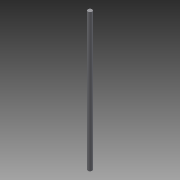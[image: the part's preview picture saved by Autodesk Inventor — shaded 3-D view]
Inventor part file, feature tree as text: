
AUTODESK INVENTOR PART (.ipt)
format: ipt  version: 2013 (Build 170138000, 138)  size: 60,416 bytes
history: native  units: in
note: dims shown in document units (in); Inventor stores cm internally (conversion verified against a paired STEP export)
features: extrude x1, sketch x1
ambient origin geometry x8: Origin, YZ Plane, XZ Plane, XY Plane, X Axis, Y Axis, Z Axis, Center Point
bodies: Solid1 (feature_tree)
feature tree (2):
  extrude  "Extrusion1"  Depth=16.25in TaperAngle=0.0deg
  sketch  "Sketch1"  dims[d0=0.5in d1=16.25in d2=0.0in]
